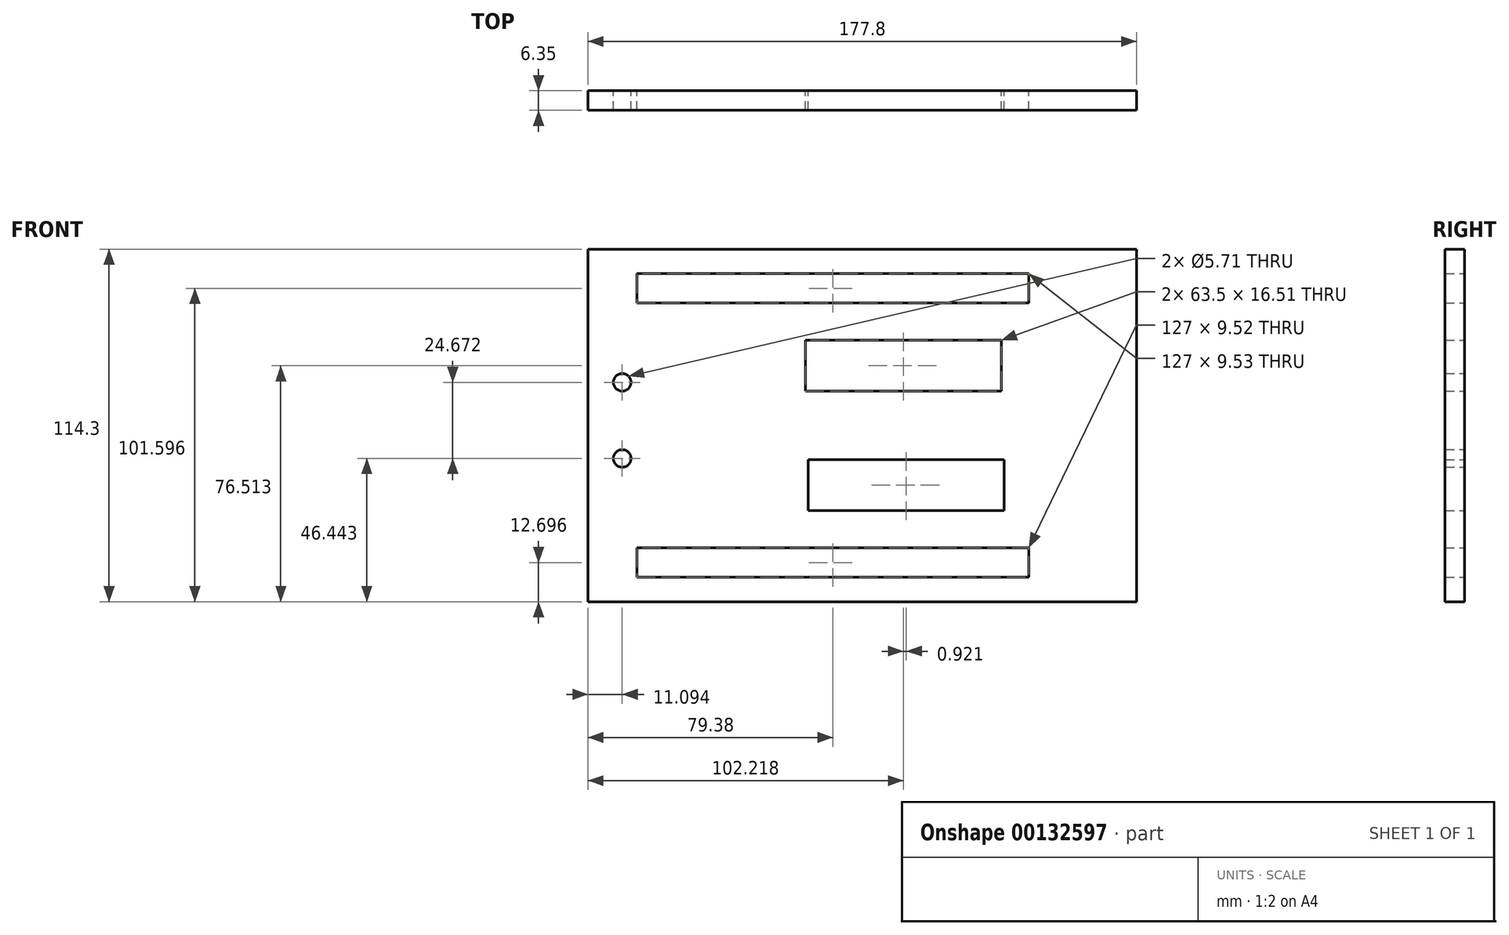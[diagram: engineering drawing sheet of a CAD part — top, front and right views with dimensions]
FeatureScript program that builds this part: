
annotation { "Feature Type Name" : "Feature", "Feature Type Description" : "" }
export const myFeature = defineFeature(function(context is Context, id is Id, definition is map)
    precondition{}
    {
        {
            var Q0;
            Q0=qCreatedBy(makeId("Front.planeOp"),FACE);
            var sketch = newSketch(context, id + "F0", { "sketchPlane" : qUnion([Q0])});
            skLineSegment(sketch, "E0.bottom", {"start": v(-79.37, 58.16) * mm, "end": v(98.43, 58.16) * mm});
            skLineSegment(sketch, "E0.top", {"start": v(-79.38, -56.14) * mm, "end": v(98.43, -56.14) * mm});
            skLineSegment(sketch, "E0.left", {"start": v(-79.37, 58.16) * mm, "end": v(-79.38, -56.14) * mm});
            skLineSegment(sketch, "E0.right", {"start": v(98.43, 58.16) * mm, "end": v(98.43, -56.14) * mm});
            skLineSegment(sketch, "E1.bottom", {"start": v(-63.5, 40.7) * mm, "end": v(63.5, 40.7) * mm});
            skLineSegment(sketch, "E1.top", {"start": v(-63.5, 50.22) * mm, "end": v(63.5, 50.22) * mm});
            skLineSegment(sketch, "E1.left", {"start": v(-63.5, 50.22) * mm, "end": v(-63.5, 40.7) * mm});
            skLineSegment(sketch, "E1.right", {"start": v(63.5, 50.22) * mm, "end": v(63.5, 40.7) * mm});
            skLineSegment(sketch, "E2.bottom", {"start": v(-63.5, -38.68) * mm, "end": v(63.5, -38.68) * mm});
            skLineSegment(sketch, "E2.top", {"start": v(-63.5, -48.2) * mm, "end": v(63.5, -48.2) * mm});
            skLineSegment(sketch, "E2.left", {"start": v(-63.5, -38.68) * mm, "end": v(-63.5, -48.2) * mm});
            skLineSegment(sketch, "E2.right", {"start": v(63.5, -38.68) * mm, "end": v(63.5, -48.2) * mm});
            skLineSegment(sketch, "E3.bottom", {"start": v(-8.91, 28.63) * mm, "end": v(54.59, 28.63) * mm});
            skLineSegment(sketch, "E3.top", {"start": v(-8.91, 12.12) * mm, "end": v(54.59, 12.12) * mm});
            skLineSegment(sketch, "E3.left", {"start": v(-8.91, 28.63) * mm, "end": v(-8.91, 12.12) * mm});
            skLineSegment(sketch, "E3.right", {"start": v(54.59, 28.63) * mm, "end": v(54.59, 12.12) * mm});
            skLineSegment(sketch, "E4.bottom", {"start": v(-8, -10.1) * mm, "end": v(55.5, -10.1) * mm});
            skLineSegment(sketch, "E4.top", {"start": v(-8, -26.62) * mm, "end": v(55.5, -26.62) * mm});
            skLineSegment(sketch, "E4.left", {"start": v(-8, -10.1) * mm, "end": v(-8, -26.62) * mm});
            skLineSegment(sketch, "E4.right", {"start": v(55.5, -10.1) * mm, "end": v(55.5, -26.62) * mm});
            skCircle(sketch, "E5", {"center": v(-68.29, 14.98) * mm, "radius": 2.86 * mm});
            skCircle(sketch, "E6", {"center": v(-68.29, -9.7) * mm, "radius": 2.86 * mm});
            skSolve(sketch);
        }
        {
            var Q0;
            Q0=makeQuery(id+"F0.imprint","IMPRINT",FACE,{"disambiguationData":[TD([[makeQuery(id+"F0.imprint","IMPRINT",EDGE,{"derivedFrom":sQuery(id+"F0.wireOp",EDGE,"E0.bottom")}),-1.0]])]});
            extrude(context, id + "F1", {"entities" : qUnion([Q0]), "depth" : 6.35 * mm});
        }
    });
